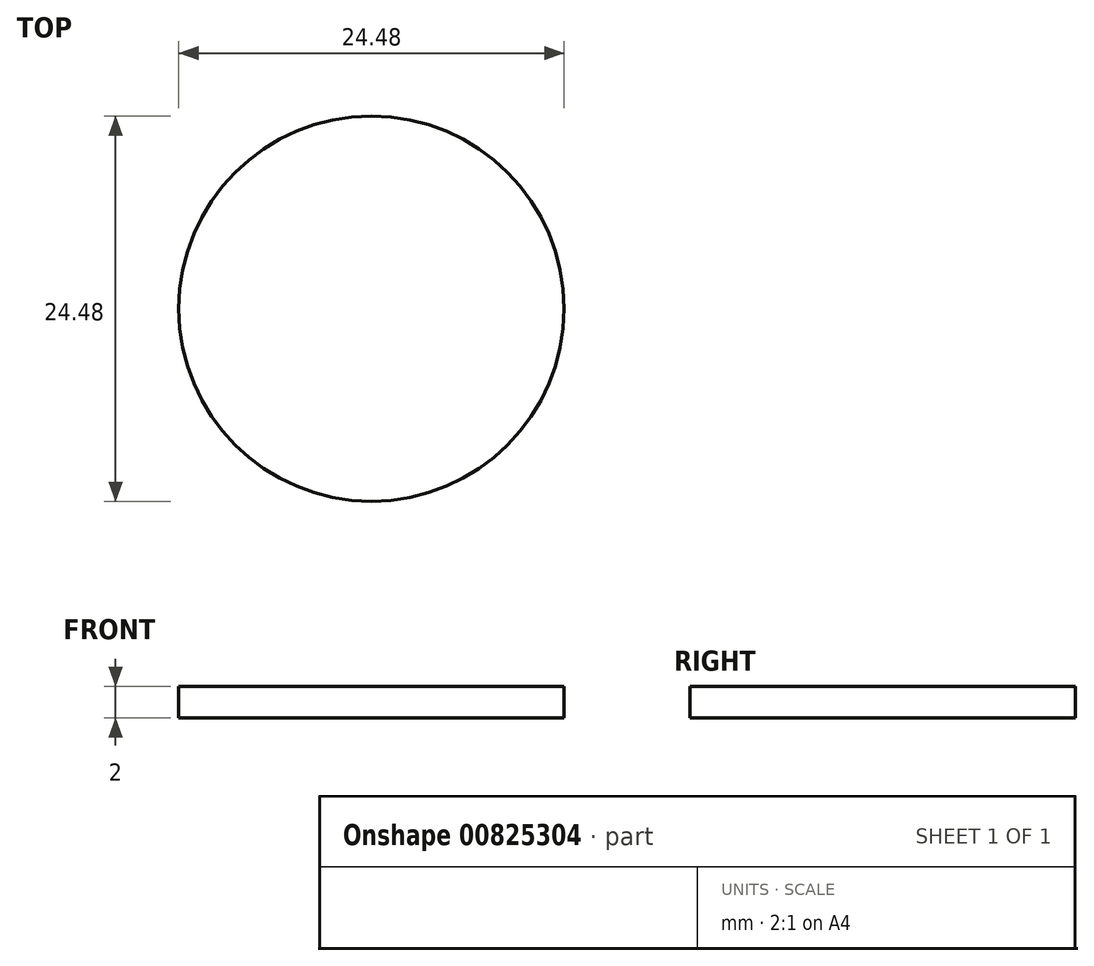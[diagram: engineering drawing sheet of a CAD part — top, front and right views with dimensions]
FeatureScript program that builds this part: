
annotation { "Feature Type Name" : "Feature", "Feature Type Description" : "" }
export const myFeature = defineFeature(function(context is Context, id is Id, definition is map)
    precondition{}
    {
        {
            var Q0;
            Q0=qCreatedBy(makeId("Top.planeOp"),FACE);
            var sketch = newSketch(context, id + "F0", { "sketchPlane" : qUnion([Q0])});
            skCircle(sketch, "E0", {"center": v(0, 0) * mm, "radius": 12.24 * mm});
            skSolve(sketch);
        }
        {
            var Q0;
            Q0 = qSketchRegion(id + "F0", true);
            extrude(context, id + "F1", {"entities" : qUnion([Q0]), "depth" : 2 * mm, "offsetDistance" : 25 * mm});
        }
    });
